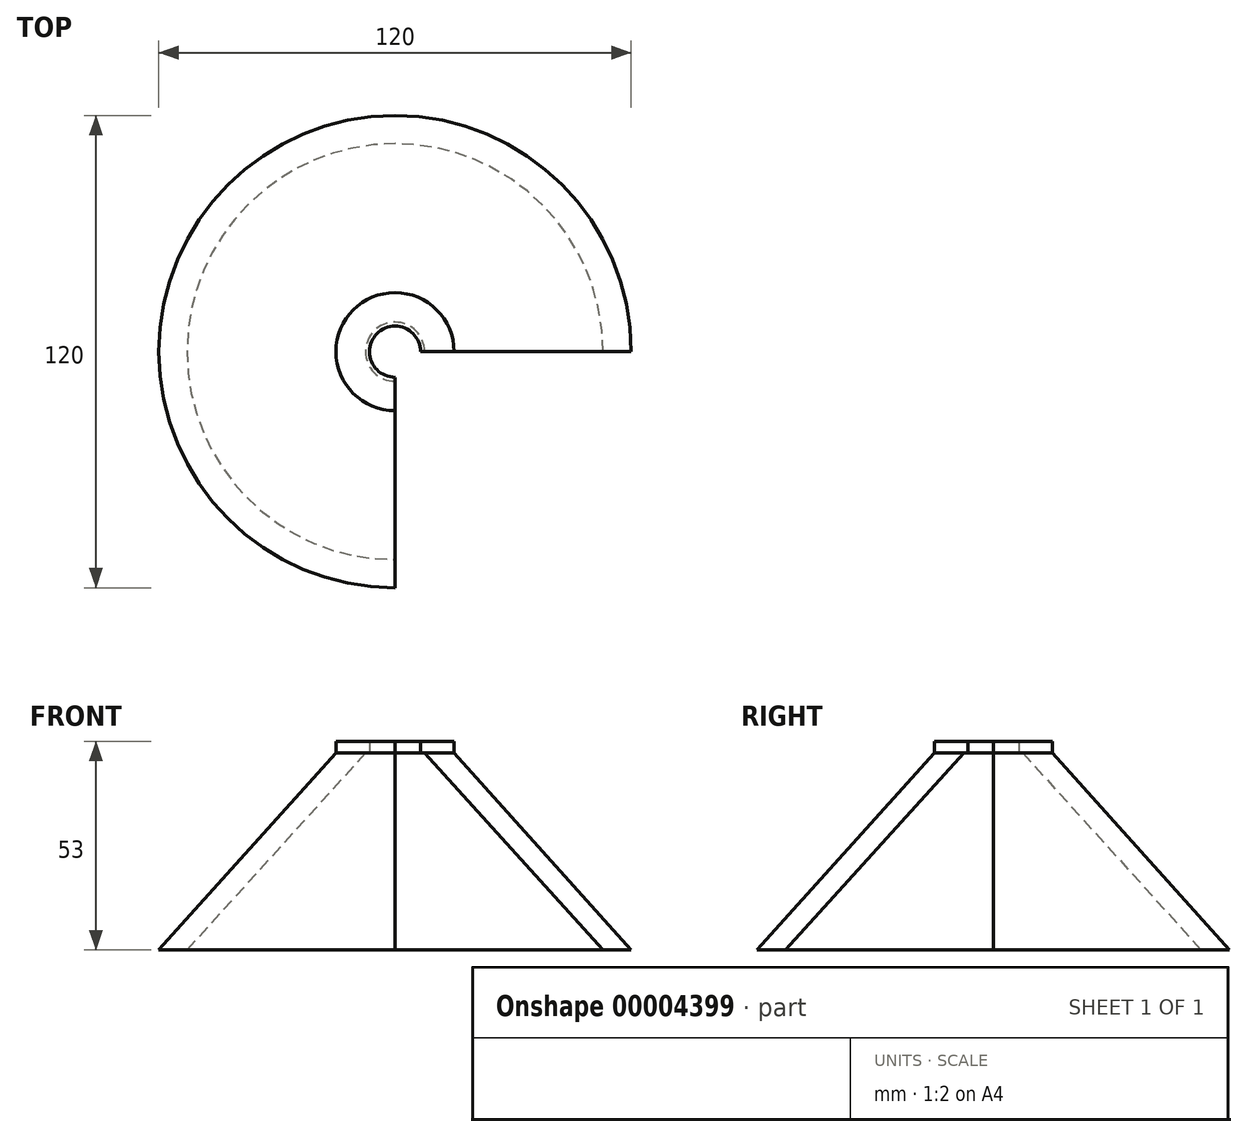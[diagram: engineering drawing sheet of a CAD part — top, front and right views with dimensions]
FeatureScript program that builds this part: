
annotation { "Feature Type Name" : "Feature", "Feature Type Description" : "" }
export const myFeature = defineFeature(function(context is Context, id is Id, definition is map)
    precondition{}
    {
        {
            var Q0;
            Q0=qCreatedBy(makeId("Top.planeOp"),FACE);
            var sketch = newSketch(context, id + "F0", { "sketchPlane" : qUnion([Q0])});
            skCircle(sketch, "E0", {"center": v(0, 0) * mm, "radius": 6.5 * mm});
            skCircle(sketch, "E1", {"center": v(0, 0) * mm, "radius": 15 * mm});
            skLineSegment(sketch, "E2", {"start": v(0, 0) * mm, "end": v(0, -15) * mm});
            skLineSegment(sketch, "E3", {"start": v(0, 0) * mm, "end": v(15, 0) * mm});
            skSolve(sketch);
        }
        {
            var Q0;
            {var subQ0=sQuery(id+"F0.wireOp",EDGE,"E2");var subQ1=sQuery(id+"F0.wireOp",EDGE,"E0");var subQ2=makeQuery(id+"F0.imprint","INTERSECT",VERTEX,{"derivedFrom":[subQ1,subQ0]});Q0=makeQuery(id+"F0.imprint","IMPRINT",FACE,{"disambiguationData":[TD([[makeQuery(id+"F0.imprint","IMPRINT",EDGE,{"disambiguationData":[TD([[subQ2,1.0]])],"derivedFrom":subQ1}),-1.0]])]});}
            extrude(context, id + "F1", {"entities" : qUnion([Q0]), "depth" : 3 * mm});
        }
        {
            var Q0;
            Q0=qCreatedBy(makeId("Front.planeOp"),FACE);
            var sketch = newSketch(context, id + "F2", { "sketchPlane" : qUnion([Q0])});
            skLineSegment(sketch, "E4", {"start": v(0, 0) * mm, "end": v(0, -50) * mm, "construction": true});
            skLineSegment(sketch, "E5", {"start": v(0, -50) * mm, "end": v(60, -50) * mm, "construction": true});
            skLineSegment(sketch, "E6", {"start": v(0, 0) * mm, "end": v(15, 0) * mm, "construction": true});
            skLineSegment(sketch, "E7", {"start": v(15, 0) * mm, "end": v(60, -50) * mm});
            skLineSegment(sketch, "E8", {"start": v(60, -50) * mm, "end": v(52.83, -50) * mm});
            skLineSegment(sketch, "E9", {"start": v(52.83, -50) * mm, "end": v(7.5, 0) * mm});
            skLineSegment(sketch, "E10", {"start": v(7.5, 0) * mm, "end": v(15, 0) * mm});
            skSolve(sketch);
        }
        {
            var Q0;
            Q0=makeQuery(id+"F2.imprint","IMPRINT",FACE,{"disambiguationData":[TD([[makeQuery(id+"F2.imprint","IMPRINT",EDGE,{"derivedFrom":sQuery(id+"F2.wireOp",EDGE,"E7")}),-1.0]])]});
            var Q1;
            Q1=sQuery(id+"F2.wireOp",EDGE,"E4");
            revolve(context, id + "F3", {"entities" : qUnion([Q0]), "axis" : qUnion([Q1]), "revolveType" : RevolveType.ONE_DIRECTION, "oppositeDirection" : true, "angle" : 270 * degree});
        }
    });
